# Revit family: Displays_Pier_ASHanging_Articulated
name_source: partatom
category: Generic Models
units: mm (PartAtom-declared; Revit-internal decimal feet)

## family parameters
Always vertical = No
Can host rebar = No
Classification Number = 23.40.90.11
Cut with Voids When Loaded = No
Maintain Annotation Orientation = No
Part Type = Normal
Room Calculation Point = No
Round Connector Dimension = Use Diameter
Shared = Yes
Work Plane-Based = Yes

## types (2) — shared parameters
Assembly Code = C1030500
CL Offset = 0' - 0 27/32"
Default Elevation = 4' - 0"
Description = AS Hanging Articulated Pier
Installation-Fabrication = https://www.ashanging.com
Keynote = 10 14 00
Manufacturer = AS Hanging
Manufacturer Website = https://www.ashanging.com
Model = Articulated Pier
Pier = Brushed Nickel
Product Data = http://www.arcat.com
Product Properties = https://www.ashanging.com
Revision = R1_2017
Sales Information = https://www.ashanging.com
Specification = http://www.arcat.com
URL = https://www.ashanging.com

## per-type parameters (varying)
| type | Cable | Cap | Height | Top | Width |
| Top | Stainless Steel | Pier_ASH_Artic-Top : Top | 0' - 2 13/64" | Yes | 0' - 0 53/64" |
| Bottom | <By Category> | Pier_ASH_Artic-Top : Bottom | 0' - 0 1/2" | No | 0' - 1" |

## geometry (parser evidence)
native form markers: Sweep x7
no freeform markers — native parametric forms only
